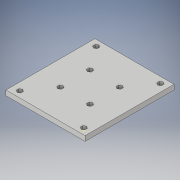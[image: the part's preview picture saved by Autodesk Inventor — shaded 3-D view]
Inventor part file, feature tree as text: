
AUTODESK INVENTOR PART (.ipt)
format: ipt  version: 2019 (Build 230136000, 136)  size: 301,568 bytes
history: native  units: in
note: dims shown in document units (in); Inventor stores cm internally (conversion verified against a paired STEP export)
features: sketch x8, extrude x6
ambient origin geometry x8: Origin, YZ Plane, XZ Plane, XY Plane, X Axis, Y Axis, Z Axis, Center Point
bodies: Solid1 (feature_tree)
feature tree (14):
  extrude  "Extrusion1"  Depth=3.5433in
  sketch  "Sketch2"  dims[d2=0.25in d3=0.0in d5=0.1181in]
  extrude  "Extrusion2"  Depth=0.25in
  extrude  "Extrusion3"  Depth=0.1181in
  extrude  "Extrusion4"  Depth=0.25in TaperAngle=0.0deg
  sketch  "Sketch6"  dims[d13=0.25in d14=0.0in d15=0.1181in d16=0.0984in d17=0.0984in d18=0.0984in]
  extrude  "Extrusion5"  Depth=4.5in
  extrude  "Extrusion6"  Depth=0.25in
  sketch  "Sketch1"  dims[d0=4.1732in d1=3.5433in]
  sketch  "Sketch3"  dims[d6=0.1181in d7=0.1181in]
  sketch  "Sketch4"  dims[d8=0.1181in d9=0.25in d10=0.0in]
  sketch  "Sketch5"  dims[d11=4.0in d12=4.5in]
  sketch  "Sketch7"  dims[d19=1.5in]
  sketch  "Sketch8"  dims[d20=1.5in d21=0.1181in d22=0.1181in d23=0.1181in d24=0.1181in d25=0.25in d26=0.0in d29=0.25in d30=0.0in d31=1.0in d32=0.0in]
